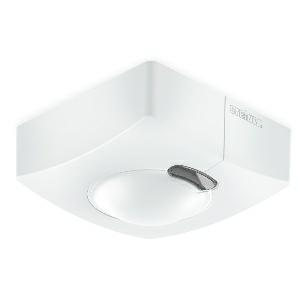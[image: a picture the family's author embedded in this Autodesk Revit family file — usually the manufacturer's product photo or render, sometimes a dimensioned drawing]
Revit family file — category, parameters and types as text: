
# Revit family: hf_3360_010546
name_source: partatom
category: Elektroinstallationen
revit_build: Autodesk Revit 2016 (Build: 20190508_0715(x64)
units: mm (PartAtom-declared; Revit-internal decimal feet)

## family parameters
Basisbauteil = Fläche
Beim Laden mit Abzugskörper schneiden = Nein
Bemaßung runder Anschluss = Durchmesser verwenden
Beschriftungsausrichtung beibehalten = Nein
Gemeinsam genutzt = Nein
Raumberechnungspunkt = Nein
Teiletyp = Normal

## types (1)
- HF 3360
    Apparent Load = 0 VA
    Beschreibung = Type: Motion detectors; Dimensions (L x W x H): 52 x 95 x 95 mm; Mains power supply: 220 – 240 V / 50 – 60 Hz; Sensor Technology: High frequency; Application, place: Indoors; Application, room: function room / ancillary room, stairwell, WC / washroom, multi-storey / underground car park, Indoors; Installation site: wall, ceiling, corner; Installation: Surface wiring; HF-system: 5,8 GHz; Electronic scalability: Yes; Mechanical scalability: No; Mounting height: 2,00 – 4,00 m; Optimum mounting height: 2,8 m; Detection: also through glass, wood and stud walls; Detection angle: 360 °; Angle of aperture: 140 °; Sneak-by guard: Yes; Reach, radial: Ø 8 m (50 m²); Reach, tangential: Ø 8 m (50 m²); Twilight setting TEACH: Yes; Twilight setting: 2 – 1000 lx; Time setting: 5 sec – 15 min; Constant-lighting control: No; Basic light level function: No; Functions: Normal / test mode, Manual ON / ON-OFF; Settings via: Remote control, Potentiometers, Smart Remote; With remote control: No; Interconnection: Yes; IP-rating: IP54; Material: Plastic; Ambient temperature: -20 – 50 °C; Colour: white; Colour, RAL: 9010; Manufacturer's Warranty: 5 years; Version: PF - surface, sq.; PU1, EAN: 4007841010546
    Height = 95 mm
    Hersteller = Steinel
    Length = 52 mm  [stored 0.170604 ft]
    ModVariant = Nein
    Modell = 010546
    Mounting Type = Surface mounted
    Number of Poles = 1
    OnlyDefault = Ja
    Power Factor = 1
    Product Name = HF 3360
    Product group = Sensor-switched indoor light
    ProductGroupID = 30
    Protection Class = Protection class
    Protection Degree = IP 54
    RlxData = <blob elided: 25705 chars, md5=a346c907>
    SensorDataFile = {"IESDataFiles":[]}
    Typenbild = produkt1_010546.jpg
    Typenkommentare = Product without accessories
    URL = http://relux.com
    VarID = ---
    Voltage = 0 V
    Vorgabe-Ansicht = 1800 mm
    Weight = 0.00 kg
    Width = 95 mm

note: [stored X ft] marks values corroborated as IEEE doubles in the binary element streams (Revit-internal decimal feet)

## geometry (parser evidence)
native form markers: Blend x4, Sweep x11
no freeform markers — native parametric forms only
